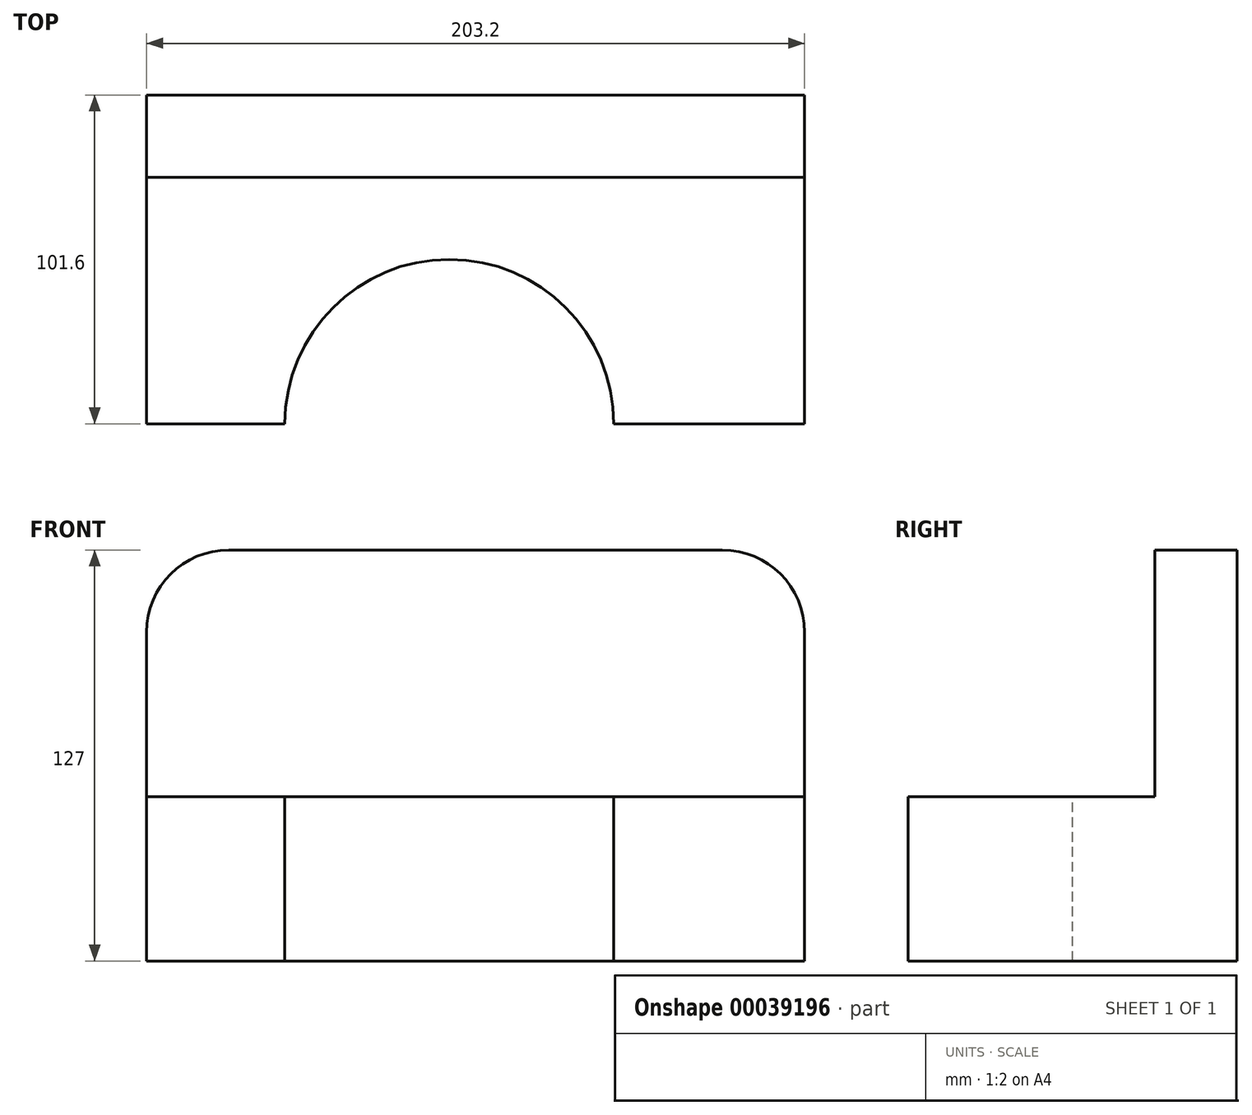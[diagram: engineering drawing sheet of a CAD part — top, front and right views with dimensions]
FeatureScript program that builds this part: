
annotation { "Feature Type Name" : "Feature", "Feature Type Description" : "" }
export const myFeature = defineFeature(function(context is Context, id is Id, definition is map)
    precondition{}
    {
        {
            var Q0;
            Q0=qCreatedBy(makeId("Top.planeOp"),FACE);
            var sketch = newSketch(context, id + "F8", { "sketchPlane" : qUnion([Q0])});
            skLineSegment(sketch, "E0.bottom", {"start": v(-45.93, 38.77) * mm, "end": v(157.27, 38.77) * mm});
            skLineSegment(sketch, "E0.top", {"start": v(-45.93, -62.83) * mm, "end": v(157.27, -62.83) * mm});
            skLineSegment(sketch, "E0.left", {"start": v(-45.93, 38.77) * mm, "end": v(-45.93, -62.83) * mm});
            skLineSegment(sketch, "E0.right", {"start": v(157.27, 38.77) * mm, "end": v(157.27, -62.83) * mm});
            skSolve(sketch);
        }
        {
            var Q0;
            Q0=qSketchRegion(id+"F8",true);
            var Q1;
            Q1=makeQuery(id+"F8.imprint","IMPRINT",FACE,{"disambiguationData":[TD([[makeQuery(id+"F8.imprint","IMPRINT",EDGE,{"derivedFrom":sQuery(id+"F8.wireOp",EDGE,"E0.bottom")}),-1.0]])]});
            extrude(context, id + "F0", {"entities" : qUnion([Q0, Q1]), "depth" : 25.4 * mm});
        }
        {
            var Q0;
            Q0=makeQuery(id+"F0.opExtrude","CAP_FACE",FACE,{"disambiguationData":[OSD([sQuery(id+"F8.wireOp",EDGE,"E0.bottom"),sQuery(id+"F8.wireOp",EDGE,"E0.top"),sQuery(id+"F8.wireOp",EDGE,"E0.left"),sQuery(id+"F8.wireOp",EDGE,"E0.right")])],"isStart":false});
            var sketch = newSketch(context, id + "F1", { "sketchPlane" : qUnion([Q0])});
            skLineSegment(sketch, "E1.bottom", {"start": v(-45.93, 38.77) * mm, "end": v(157.27, 38.77) * mm});
            skLineSegment(sketch, "E1.top", {"start": v(-45.93, 13.37) * mm, "end": v(157.27, 13.37) * mm});
            skLineSegment(sketch, "E1.left", {"start": v(-45.93, 38.77) * mm, "end": v(-45.93, 13.37) * mm});
            skLineSegment(sketch, "E1.right", {"start": v(157.27, 38.77) * mm, "end": v(157.27, 13.37) * mm});
            skSolve(sketch);
        }
        {
            var Q0;
            Q0=qSketchRegion(id+"F1",true);
            var Q1;
            Q1=makeQuery(id+"F1.imprint","IMPRINT",FACE,{"disambiguationData":[TD([[makeQuery(id+"F1.imprint","IMPRINT",EDGE,{"derivedFrom":sQuery(id+"F1.wireOp",EDGE,"E1.bottom")}),-1.0]])]});
            extrude(context, id + "F2", {"entities" : qUnion([Q0, Q1]), "operationType" : NewBodyOperationType.ADD, "depth" : 101.6 * mm});
        }
        {
            var Q0;
            Q0=makeQuery(id+"F2.opExtrude","SWEPT_FACE",FACE,{"disambiguationData":[OSD([sQuery(id+"F1.wireOp",EDGE,"E1.top")])]});
            var sketch = newSketch(context, id + "F3", { "sketchPlane" : qUnion([Q0])});
            skLineSegment(sketch, "E2", {"start": v(157.27, 127) * mm, "end": v(131.87, 127) * mm});
            skLineSegment(sketch, "E3", {"start": v(131.87, 127) * mm, "end": v(131.87, 101.6) * mm});
            skCircle(sketch, "E4", {"center": v(131.87, 101.6) * mm, "radius": 25.4 * mm});
            skSolve(sketch);
        }
        {
            var Q0;
            {var subQ4=sQuery(id+"F3.wireOp",EDGE,"E2");Q0=makeQuery(id+"F3.imprint","IMPRINT",FACE,{"disambiguationData":[TD([[makeQuery(id+"F3.imprint","IMPRINT",EDGE,{"derivedFrom":subQ4}),-1.0]])]});}
            extrude(context, id + "F9", {"entities" : qUnion([Q0]), "operationType" : NewBodyOperationType.REMOVE, "oppositeDirection" : true, "depth" : 25.4 * mm});
        }
        {
            var Q0;
            Q0=makeQuery(id+"F2.opExtrude","CAP_EDGE",EDGE,{"disambiguationData":[OSD([sQuery(id+"F1.wireOp",EDGE,"E1.left")])],"isStart":false});
            fillet(context, id + "F4", {"entities" : qUnion([Q0]), "radius" : 25.4 * mm, "tangentPropagation" : true, "allowEdgeOverflow" : false});
        }
        {
            var Q0;
            Q0=makeQuery(id+"F0.opExtrude","CAP_FACE",FACE,{"disambiguationData":[OSD([sQuery(id+"F8.wireOp",EDGE,"E0.bottom"),sQuery(id+"F8.wireOp",EDGE,"E0.top"),sQuery(id+"F8.wireOp",EDGE,"E0.left"),sQuery(id+"F8.wireOp",EDGE,"E0.right")])],"isStart":false});
            var sketch = newSketch(context, id + "F5", { "sketchPlane" : qUnion([Q0])});
            skCircle(sketch, "E5", {"center": v(47.56, -62.83) * mm, "radius": 50.8 * mm});
            skSolve(sketch);
        }
        {
            var Q0;
            Q0=qSketchRegion(id+"F5",true);
            extrude(context, id + "F6", {"entities" : qUnion([Q0]), "operationType" : NewBodyOperationType.REMOVE, "oppositeDirection" : true, "depth" : 25.4 * mm});
        }
        {
            var Q0;
            Q0=makeQuery(id+"F0.opExtrude","CAP_FACE",FACE,{"disambiguationData":[OSD([sQuery(id+"F8.wireOp",EDGE,"E0.bottom"),sQuery(id+"F8.wireOp",EDGE,"E0.top"),sQuery(id+"F8.wireOp",EDGE,"E0.left"),sQuery(id+"F8.wireOp",EDGE,"E0.right")])],"isStart":false});
            extrude(context, id + "F7", {"entities" : qUnion([Q0]), "operationType" : NewBodyOperationType.ADD, "depth" : 25.4 * mm});
        }
    });
